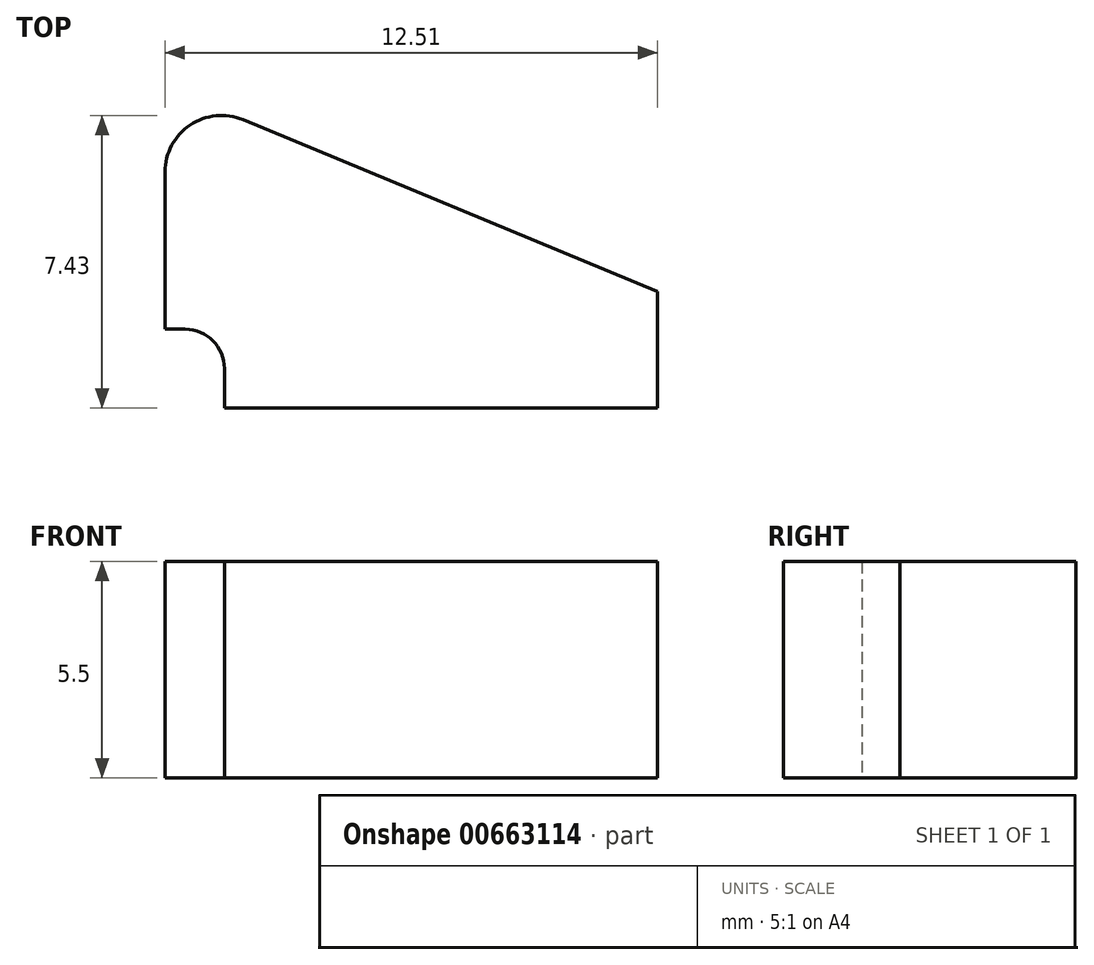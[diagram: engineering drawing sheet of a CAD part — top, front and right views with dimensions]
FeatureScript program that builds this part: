
annotation { "Feature Type Name" : "Feature", "Feature Type Description" : "" }
export const myFeature = defineFeature(function(context is Context, id is Id, definition is map)
    precondition{}
    {
        {
            var Q0;
            Q0=qCreatedBy(makeId("Top.planeOp"),FACE);
            var sketch = newSketch(context, id + "F0", { "sketchPlane" : qUnion([Q0])});
            skLineSegment(sketch, "E0", {"start": v(-8.5, 5) * mm, "end": v(-8.5, 1) * mm});
            skLineSegment(sketch, "E1.top", {"start": v(-8.5, 1) * mm, "end": v(-7, 1) * mm});
            skLineSegment(sketch, "E1.right", {"start": v(-7, -1) * mm, "end": v(-7, 1) * mm});
            skLineSegment(sketch, "E2", {"start": v(4, -1) * mm, "end": v(4, 1.96) * mm});
            skLineSegment(sketch, "E3", {"start": v(4, 1.96) * mm, "end": v(-6.53, 6.32) * mm});
            skArc(sketch, "E4", {"start": v(-6.53, 6.32) * mm, "mid": v(-7.87, 6.19) * mm, "end": v(-8.5, 5) * mm});
            skLineSegment(sketch, "E5", {"start": v(-7, -1) * mm, "end": v(4, -1) * mm});
            skSolve(sketch);
        }
        {
            var Q0;
            Q0=makeQuery(id+"F0.imprint","IMPRINT",FACE,{"disambiguationData":[TD([[makeQuery(id+"F0.imprint","IMPRINT",EDGE,{"derivedFrom":sQuery(id+"F0.wireOp",EDGE,"E0")}),1.0]])]});
            extrude(context, id + "F1", {"entities" : qUnion([Q0]), "endBound" : BoundingType.SYMMETRIC, "depth" : 5.5 * mm, "offsetDistance" : 25 * mm});
        }
        {
            var Q0;
            Q0=makeQuery(id+"F1.opExtrude","SWEPT_EDGE",EDGE,{"disambiguationData":[OSD([sQuery(id+"F0.wireOp",EDGE,"E1.top"),sQuery(id+"F0.wireOp",EDGE,"E1.right")])]});
            fillet(context, id + "F2", {"entities" : qUnion([Q0]), "radius" : 1 * mm, "tangentPropagation" : true, "allowEdgeOverflow" : false});
        }
    });
